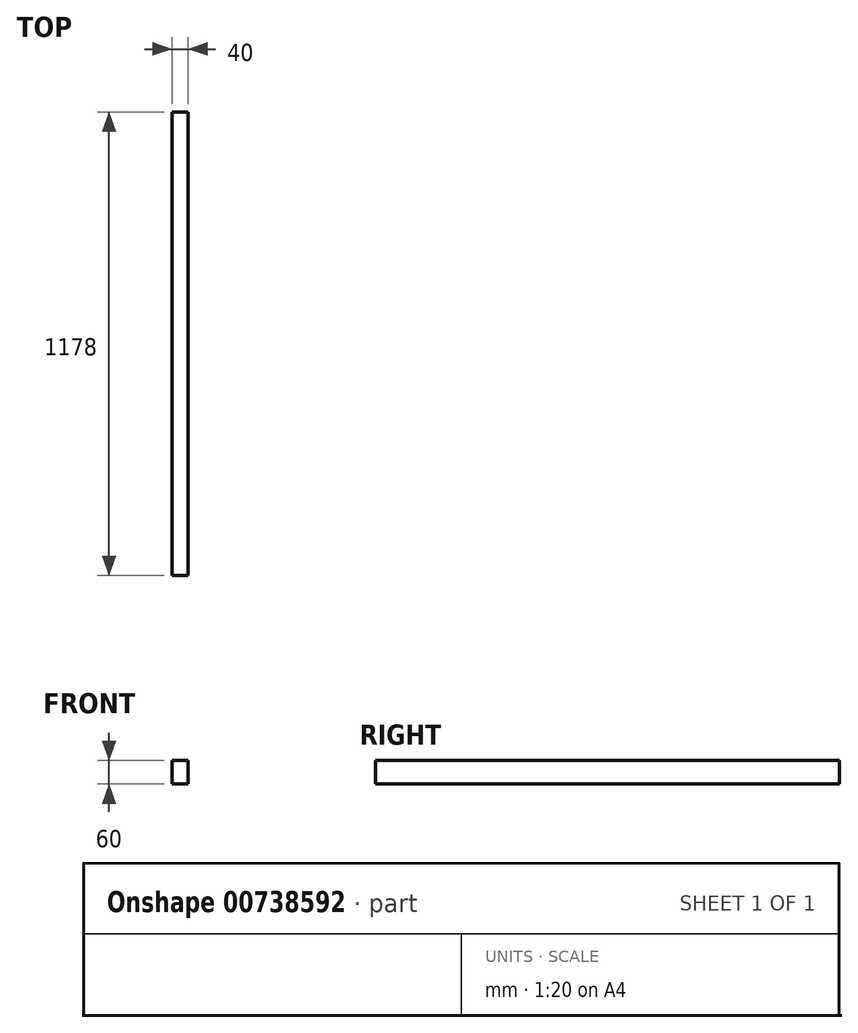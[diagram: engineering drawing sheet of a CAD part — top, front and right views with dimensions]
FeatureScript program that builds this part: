
annotation { "Feature Type Name" : "Feature", "Feature Type Description" : "" }
export const myFeature = defineFeature(function(context is Context, id is Id, definition is map)
    precondition{}
    {
        {
            var Q0;
            Q0=qCreatedBy(makeId("Top.planeOp"),FACE);
            var sketch = newSketch(context, id + "F0", { "sketchPlane" : qUnion([Q0])});
            skLineSegment(sketch, "E0.bottom", {"start": v(20, -589) * mm, "end": v(-20, -589) * mm});
            skLineSegment(sketch, "E0.top", {"start": v(20, 589) * mm, "end": v(-20, 589) * mm});
            skLineSegment(sketch, "E0.left", {"start": v(20, -589) * mm, "end": v(20, 589) * mm});
            skLineSegment(sketch, "E0.right", {"start": v(-20, -589) * mm, "end": v(-20, 589) * mm});
            skPoint(sketch, "E0.middle", {"position": v(0, 0) * mm});
            skSolve(sketch);
        }
        {
            var Q0;
            Q0 = qSketchRegion(id + "F0", true);
            extrude(context, id + "F1", {"entities" : qUnion([Q0]), "depth" : 60 * mm, "offsetDistance" : 25 * mm});
        }
    });
